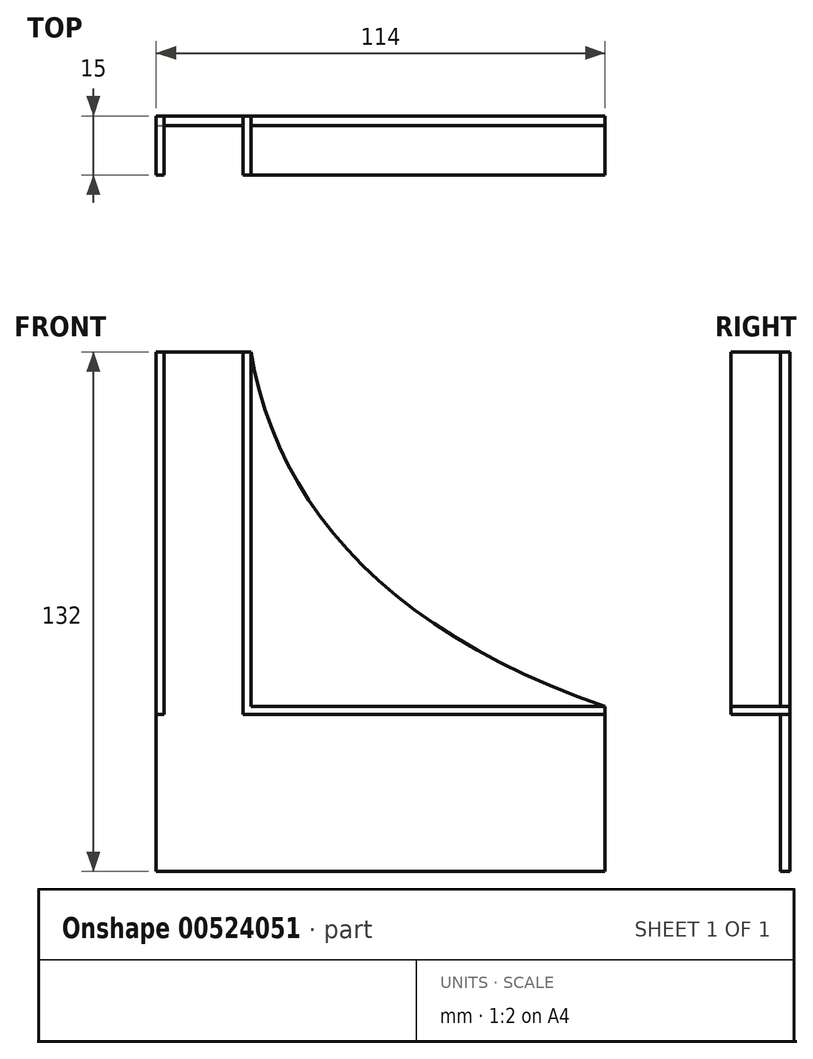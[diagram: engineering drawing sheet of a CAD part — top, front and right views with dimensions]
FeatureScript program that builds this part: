
annotation { "Feature Type Name" : "Feature", "Feature Type Description" : "" }
export const myFeature = defineFeature(function(context is Context, id is Id, definition is map)
    precondition{}
    {
        {
            var Q0;
            Q0=qCreatedBy(makeId("Front.planeOp"),FACE);
            var sketch = newSketch(context, id + "F0", { "sketchPlane" : qUnion([Q0])});
            skLineSegment(sketch, "E0", {"start": v(-42.98, 63.05) * mm, "end": v(-42.98, -26.95) * mm});
            skLineSegment(sketch, "E1", {"start": v(47.02, -26.95) * mm, "end": v(-42.98, -26.95) * mm});
            skLineSegment(sketch, "E2", {"start": v(47.02, -26.95) * mm, "end": v(47.02, -68.95) * mm});
            skLineSegment(sketch, "E3", {"start": v(-66.98, -68.95) * mm, "end": v(47.02, -68.95) * mm});
            skLineSegment(sketch, "E4", {"start": v(-66.98, -68.95) * mm, "end": v(-66.98, -28.95) * mm});
            skLineSegment(sketch, "E5", {"start": v(-66.98, -28.95) * mm, "end": v(47.02, -28.95) * mm});
            skLineSegment(sketch, "E6", {"start": v(-66.98, 63.05) * mm, "end": v(-66.98, -28.95) * mm});
            skLineSegment(sketch, "E7", {"start": v(-44.98, -28.95) * mm, "end": v(-44.98, 63.05) * mm});
            skLineSegment(sketch, "E8", {"start": v(-64.98, 63.05) * mm, "end": v(-64.98, -28.95) * mm});
            skLineSegment(sketch, "E9", {"start": v(-66.98, 63.05) * mm, "end": v(-64.98, 63.05) * mm});
            skLineSegment(sketch, "E10", {"start": v(-64.98, 63.05) * mm, "end": v(-44.98, 63.05) * mm});
            skLineSegment(sketch, "E11", {"start": v(-44.98, 63.05) * mm, "end": v(-42.98, 63.05) * mm});
            skFitSpline(sketch, "E12", {"points": [v(-42.98, 63.05) * mm, v(47.02, -26.95) * mm], "startDerivative": vector(19.57, -114.78) * mm, "endDerivative": vector(168.26, -57.4) * mm});
            skSolve(sketch);
        }
        {
            var Q0;
            Q0=makeQuery(id+"F0.imprint","IMPRINT",FACE,{"disambiguationData":[TD([[makeQuery(id+"F0.imprint","IMPRINT",EDGE,{"derivedFrom":sQuery(id+"F0.wireOp",EDGE,"E0")}),1.0]])]});
            var Q1;
            {var subQ3=sQuery(id+"F0.wireOp",EDGE,"E3");Q1=makeQuery(id+"F0.imprint","IMPRINT",FACE,{"disambiguationData":[TD([[makeQuery(id+"F0.imprint","IMPRINT",EDGE,{"derivedFrom":subQ3}),1.0]])]});}
            var Q2;
            {var subQ0=sQuery(id+"F0.wireOp",EDGE,"E7");Q2=makeQuery(id+"F0.imprint","IMPRINT",FACE,{"disambiguationData":[TD([[makeQuery(id+"F0.imprint","IMPRINT",EDGE,{"derivedFrom":subQ0}),1.0]])]});}
            extrude(context, id + "F1", {"entities" : qUnion([Q0, Q1, Q2]), "depth" : 2.5 * mm, "offsetDistance" : 25 * mm});
        }
        {
            var Q0;
            {var subQ0=sQuery(id+"F0.wireOp",EDGE,"E6");Q0=makeQuery(id+"F0.imprint","IMPRINT",FACE,{"disambiguationData":[TD([[makeQuery(id+"F0.imprint","IMPRINT",EDGE,{"derivedFrom":subQ0}),1.0]])]});}
            var Q1;
            Q1=makeQuery(id+"F0.imprint","IMPRINT",FACE,{"disambiguationData":[TD([[makeQuery(id+"F0.imprint","IMPRINT",EDGE,{"derivedFrom":sQuery(id+"F0.wireOp",EDGE,"E0")}),-1.0]])]});
            extrude(context, id + "F2", {"entities" : qUnion([Q0, Q1]), "depth" : 15 * mm, "offsetDistance" : 25 * mm});
        }
    });
